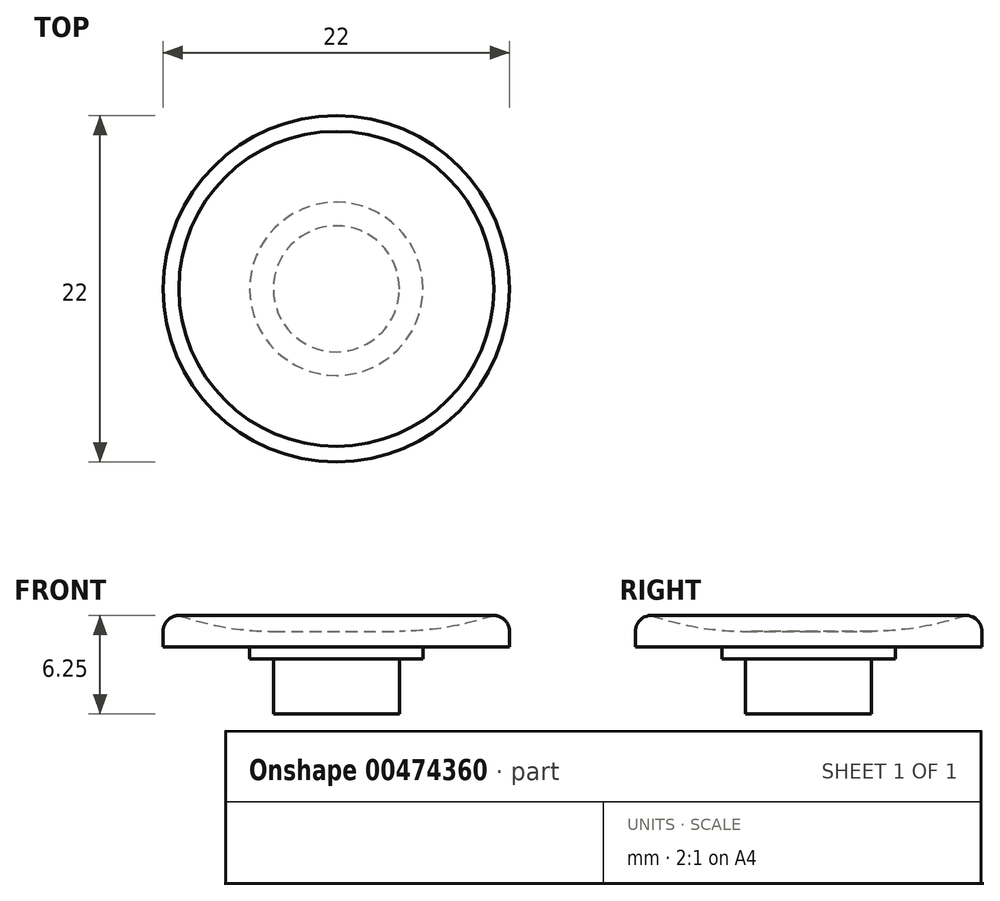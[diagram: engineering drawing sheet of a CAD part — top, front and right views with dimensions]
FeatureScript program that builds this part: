
annotation { "Feature Type Name" : "Feature", "Feature Type Description" : "" }
export const myFeature = defineFeature(function(context is Context, id is Id, definition is map)
    precondition{}
    {
        {
            var Q0;
            Q0=qCreatedBy(makeId("Front.planeOp"),FACE);
            var sketch = newSketch(context, id + "F0", { "sketchPlane" : qUnion([Q0])});
            skLineSegment(sketch, "E0", {"start": v(0, 0) * mm, "end": v(4, 0) * mm});
            skLineSegment(sketch, "E1", {"start": v(4, 0) * mm, "end": v(4, 3.5) * mm});
            skLineSegment(sketch, "E2", {"start": v(11, 4.25) * mm, "end": v(11, 5.25) * mm});
            skLineSegment(sketch, "E3", {"start": v(0, 0) * mm, "end": v(0, 5.25) * mm});
            skPoint(sketch, "E4.visualSharp", {"position": v(11, 2706.94) * mm});
            skArc(sketch, "E4.filletArc", {"start": v(11, 5.25) * mm, "mid": v(10.7, 5.96) * mm, "end": v(10, 6.25) * mm});
            skLineSegment(sketch, "E5", {"start": v(0, 5.25) * mm, "end": v(4, 5.25) * mm});
            skLineSegment(sketch, "E6", {"start": v(10, 6.25) * mm, "end": v(10, 6.25) * mm});
            skLineSegment(sketch, "E7", {"start": v(4, 3.5) * mm, "end": v(5.5, 3.5) * mm});
            skLineSegment(sketch, "E8", {"start": v(5.5, 3.5) * mm, "end": v(5.5, 4.25) * mm});
            skLineSegment(sketch, "E9", {"start": v(5.5, 4.25) * mm, "end": v(11, 4.25) * mm});
            skLineSegment(sketch, "E10", {"start": v(10, 6.25) * mm, "end": v(0, 6.25) * mm, "construction": true});
            skArc(sketch, "E11", {"start": v(4, 5.25) * mm, "mid": v(7.04, 5.5) * mm, "end": v(10, 6.25) * mm});
            skSolve(sketch);
        }
        {
            var Q0;
            Q0 = qSketchRegion(id + "F0", true);
            var Q1;
            Q1=sQuery(id+"F0.wireOp",EDGE,"E3");
            revolve(context, id + "F1", {"entities" : qUnion([Q0]), "axis" : qUnion([Q1]), "revolveType" : RevolveType.FULL});
        }
    });
